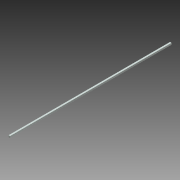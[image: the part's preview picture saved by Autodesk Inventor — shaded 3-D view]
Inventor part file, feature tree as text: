
AUTODESK INVENTOR PART (.ipt)
format: ipt  version: 2013 (Build 170138000, 138)  size: 146,944 bytes
history: native  units: in
note: dims shown in document units (in); Inventor stores cm internally (conversion verified against a paired STEP export)
features: sketch x2, plane x2, extrude x1, revolve x1, mirror x1, other x1
ambient origin geometry x8: Origin, YZ Plane, XZ Plane, XY Plane, X Axis, Y Axis, Z Axis, Center Point
bodies: Solid1 (feature_tree)
feature tree (8):
  sketch  "Sketch1"  dims[d0=12.0in d1=0.0in d2=90.0deg]
  extrude  "Extrusion1"  TaperAngle=90.0deg  [1 undecoded]
  plane  "Work Plane1"
  revolve  "Revolution1"  [1 undecoded]
  plane  "Work Plane2"
  mirror  "Mirror1"
  other  "Work Axis1"
  sketch  "Sketch2"  dims[d3=90.0deg]
note: 2 required parameter values undecoded (feature->parameter linkage not recoverable at this tier; creation-order binding heuristic only, values carry confidence <= 0.55)
